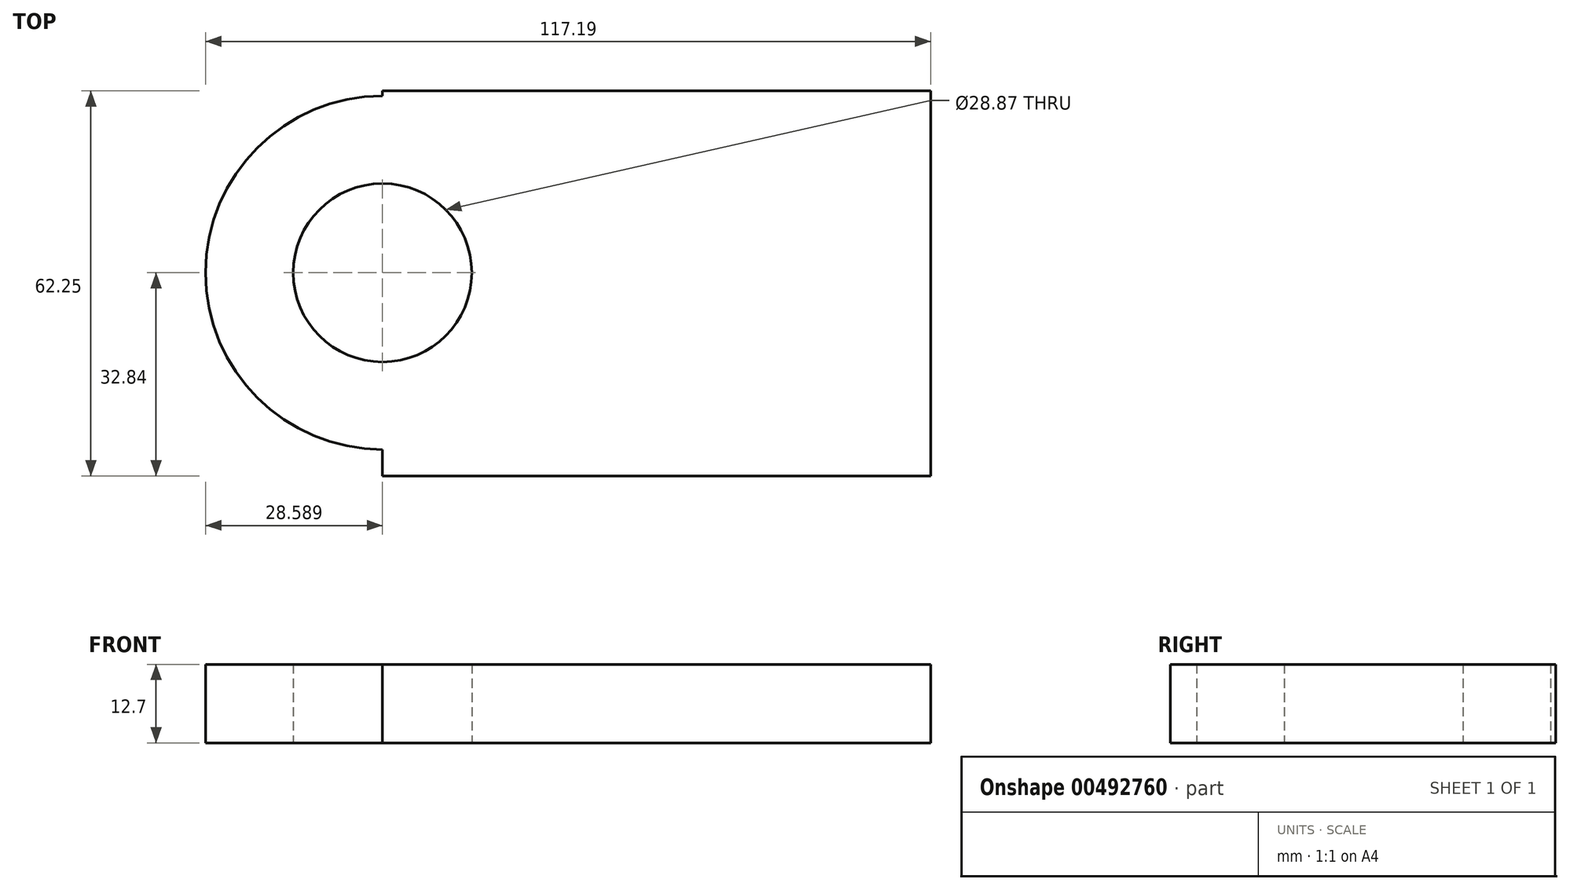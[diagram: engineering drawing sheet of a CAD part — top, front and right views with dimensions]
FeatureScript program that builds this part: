
annotation { "Feature Type Name" : "Feature", "Feature Type Description" : "" }
export const myFeature = defineFeature(function(context is Context, id is Id, definition is map)
    precondition{}
    {
        {
            var Q0;
            Q0=qCreatedBy(makeId("Top.planeOp"),FACE);
            var sketch = newSketch(context, id + "F0", { "sketchPlane" : qUnion([Q0])});
            skLineSegment(sketch, "E0.bottom", {"start": v(44.3, -32.84) * mm, "end": v(-44.3, -32.84) * mm});
            skLineSegment(sketch, "E0.top", {"start": v(44.3, 29.4) * mm, "end": v(-44.3, 29.4) * mm});
            skLineSegment(sketch, "E0.left", {"start": v(44.3, -32.84) * mm, "end": v(44.3, 29.4) * mm});
            skLineSegment(sketch, "E0.right", {"start": v(-44.3, -32.84) * mm, "end": v(-44.3, 29.4) * mm});
            skPoint(sketch, "E0.middle", {"position": v(0, -1.72) * mm});
            skCircle(sketch, "E1", {"center": v(-44.3, 0) * mm, "radius": 28.6 * mm});
            skCircle(sketch, "E2", {"center": v(-44.3, 0) * mm, "radius": 14.43 * mm});
            skSolve(sketch);
        }
        {
            var Q0;
            Q0 = qSketchRegion(id + "F0", true);
            extrude(context, id + "F1", {"entities" : qUnion([Q0]), "depth" : 12.7 * mm});
        }
    });
